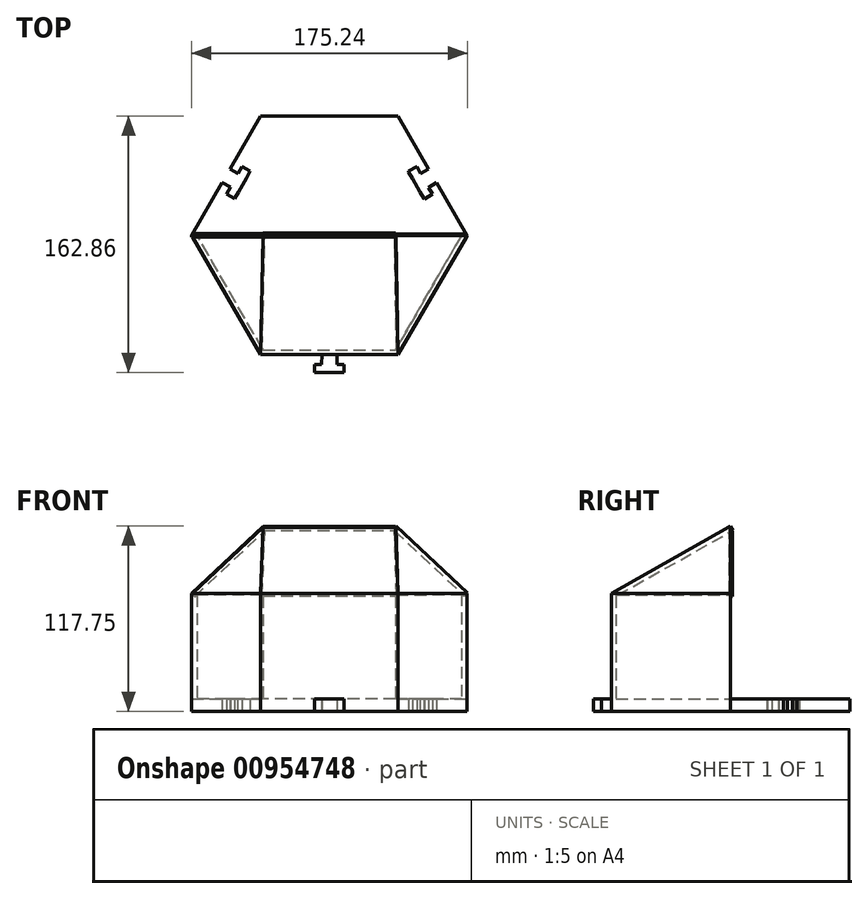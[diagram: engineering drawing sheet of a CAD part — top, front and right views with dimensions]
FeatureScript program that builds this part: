
annotation { "Feature Type Name" : "Feature", "Feature Type Description" : "" }
export const myFeature = defineFeature(function(context is Context, id is Id, definition is map)
    precondition{}
    {
        {
            var Q0;
            Q0=qCreatedBy(makeId("Top.planeOp"),FACE);
            var sketch = newSketch(context, id + "F0", { "sketchPlane" : qUnion([Q0])});
            skCircle(sketch, "E0.cCircle", {"center": v(0, 0) * mm, "radius": 75.78 * mm, "construction": true});
            skLineSegment(sketch, "E0.0", {"start": v(-43.75, 75.78) * mm, "end": v(43.75, 75.78) * mm});
            skLineSegment(sketch, "E0.1", {"start": v(43.75, 75.78) * mm, "end": v(87.5, 0) * mm});
            skLineSegment(sketch, "E0.2", {"start": v(87.5, 0) * mm, "end": v(43.75, -75.78) * mm});
            skLineSegment(sketch, "E0.3", {"start": v(43.75, -75.78) * mm, "end": v(-43.75, -75.78) * mm});
            skLineSegment(sketch, "E0.4", {"start": v(-43.75, -75.78) * mm, "end": v(-87.5, 0) * mm});
            skLineSegment(sketch, "E0.5", {"start": v(-87.5, 0) * mm, "end": v(-43.75, 75.78) * mm});
            skPoint(sketch, "E0.0.midPoint", {"position": v(0, 75.78) * mm});
            skLineSegment(sketch, "E1.0", {"start": v(-84.04, 0) * mm, "end": v(-42.02, 72.78) * mm});
            skLineSegment(sketch, "E1.1", {"start": v(42.02, 72.78) * mm, "end": v(84.04, 0) * mm});
            skLineSegment(sketch, "E1.2", {"start": v(84.04, 0) * mm, "end": v(42.02, -72.78) * mm});
            skLineSegment(sketch, "E1.3", {"start": v(-42.02, 72.78) * mm, "end": v(42.02, 72.78) * mm});
            skLineSegment(sketch, "E1.4", {"start": v(42.02, -72.78) * mm, "end": v(-42.02, -72.78) * mm});
            skLineSegment(sketch, "E1.5", {"start": v(-42.02, -72.78) * mm, "end": v(-84.04, 0) * mm});
            skLineSegment(sketch, "E2", {"start": v(-87.5, 0) * mm, "end": v(-84.04, 0) * mm});
            skLineSegment(sketch, "E3", {"start": v(84.04, 0) * mm, "end": v(87.5, 0) * mm});
            skLineSegment(sketch, "E4", {"start": v(0, 0) * mm, "end": v(0, 72.78) * mm, "construction": true});
            skLineSegment(sketch, "E5", {"start": v(0, 0) * mm, "end": v(42.02, 72.78) * mm, "construction": true});
            skLineSegment(sketch, "E6", {"start": v(0, 0) * mm, "end": v(-42.02, 72.78) * mm, "construction": true});
            skLineSegment(sketch, "E7", {"start": v(0, 36.39) * mm, "end": v(0, 72.78) * mm, "construction": true});
            skLineSegment(sketch, "E8.bottom", {"start": v(25, 48.33) * mm, "end": v(-25, 48.33) * mm});
            skLineSegment(sketch, "E8.top", {"start": v(25, 60.83) * mm, "end": v(-25, 60.83) * mm});
            skLineSegment(sketch, "E8.left", {"start": v(25, 48.33) * mm, "end": v(25, 60.83) * mm});
            skLineSegment(sketch, "E8.right", {"start": v(-25, 48.33) * mm, "end": v(-25, 60.83) * mm});
            skPoint(sketch, "E8.middle", {"position": v(0, 54.58) * mm});
            skLineSegment(sketch, "E9", {"start": v(-65.63, 37.89) * mm, "end": v(-55.16, 32) * mm, "construction": true});
            skLineSegment(sketch, "E10", {"start": v(-55.16, 32) * mm, "end": v(-52.71, 36.37) * mm, "construction": true});
            skLineSegment(sketch, "E11", {"start": v(-55.16, 32) * mm, "end": v(-57.62, 27.65) * mm, "construction": true});
            skLineSegment(sketch, "E12", {"start": v(-52.71, 36.37) * mm, "end": v(-63.12, 42.22) * mm});
            skLineSegment(sketch, "E13", {"start": v(-57.62, 27.65) * mm, "end": v(-52.71, 36.37) * mm});
            skLineSegment(sketch, "E14", {"start": v(-65.63, 37.89) * mm, "end": v(-68.13, 33.56) * mm});
            skLineSegment(sketch, "E15", {"start": v(-57.62, 27.65) * mm, "end": v(-68.13, 33.56) * mm});
            skLineSegment(sketch, "E16.MirrorCS", {"start": v(55.16, 32) * mm, "end": v(57.62, 27.65) * mm});
            skLineSegment(sketch, "E17.MirrorCS", {"start": v(55.16, 32) * mm, "end": v(52.71, 36.37) * mm});
            skLineSegment(sketch, "E18.MirrorCS", {"start": v(57.62, 27.65) * mm, "end": v(68.13, 33.56) * mm});
            skLineSegment(sketch, "E19.MirrorCS", {"start": v(87.5, 0) * mm, "end": v(43.75, 75.78) * mm});
            skLineSegment(sketch, "E20.MirrorCS", {"start": v(52.71, 36.37) * mm, "end": v(63.12, 42.22) * mm});
            skLineSegment(sketch, "E21", {"start": v(-62.87, 30.6) * mm, "end": v(-65.32, 26.25) * mm});
            skLineSegment(sketch, "E22", {"start": v(-57.62, 27.65) * mm, "end": v(-60.07, 23.3) * mm});
            skLineSegment(sketch, "E23", {"start": v(-65.32, 26.25) * mm, "end": v(-60.07, 23.3) * mm});
            skLineSegment(sketch, "E24.MirrorCS", {"start": v(-52.71, 36.37) * mm, "end": v(-50.26, 40.72) * mm});
            skLineSegment(sketch, "E25.MirrorCS", {"start": v(-57.97, 39.32) * mm, "end": v(-55.52, 43.68) * mm});
            skLineSegment(sketch, "E26.MirrorCS", {"start": v(-55.52, 43.68) * mm, "end": v(-50.26, 40.72) * mm});
            skLineSegment(sketch, "E27.MirrorCS", {"start": v(57.97, 39.32) * mm, "end": v(55.52, 43.68) * mm});
            skLineSegment(sketch, "E28.MirrorCS", {"start": v(55.52, 43.68) * mm, "end": v(50.26, 40.72) * mm});
            skLineSegment(sketch, "E29.MirrorCS", {"start": v(52.71, 36.37) * mm, "end": v(50.26, 40.72) * mm});
            skLineSegment(sketch, "E30.MirrorCS", {"start": v(57.62, 27.65) * mm, "end": v(60.07, 23.3) * mm});
            skLineSegment(sketch, "E31.MirrorCS", {"start": v(62.87, 30.6) * mm, "end": v(65.32, 26.25) * mm});
            skLineSegment(sketch, "E32.MirrorCS", {"start": v(65.32, 26.25) * mm, "end": v(60.07, 23.3) * mm});
            skLineSegment(sketch, "E33", {"start": v(-68.13, 33.56) * mm, "end": v(-65.5, 32.09) * mm});
            skLineSegment(sketch, "E34", {"start": v(68.13, 33.56) * mm, "end": v(65.5, 32.09) * mm});
            skLineSegment(sketch, "E35.1.10", {"start": v(0, 0) * mm, "end": v(-63.03, -36.39) * mm, "construction": true});
            skLineSegment(sketch, "E35.2.0", {"start": v(57.85, 27.47) * mm, "end": v(68.13, 33.56) * mm});
            skLineSegment(sketch, "E35.2.1", {"start": v(52.75, 36.07) * mm, "end": v(63.13, 42.22) * mm});
            skLineSegment(sketch, "E35.2.2", {"start": v(57.94, 39.15) * mm, "end": v(55.39, 43.45) * mm});
            skLineSegment(sketch, "E35.2.3", {"start": v(55.39, 43.45) * mm, "end": v(50.2, 40.37) * mm});
            skLineSegment(sketch, "E35.2.4", {"start": v(52.75, 36.07) * mm, "end": v(50.2, 40.37) * mm});
            skLineSegment(sketch, "E35.2.5", {"start": v(55.3, 31.77) * mm, "end": v(52.75, 36.07) * mm, "construction": true});
            skLineSegment(sketch, "E35.2.6", {"start": v(55.3, 31.77) * mm, "end": v(57.85, 27.47) * mm, "construction": true});
            skLineSegment(sketch, "E35.2.7", {"start": v(57.85, 27.47) * mm, "end": v(60.4, 23.17) * mm});
            skLineSegment(sketch, "E35.2.8", {"start": v(65.59, 26.24) * mm, "end": v(60.4, 23.17) * mm});
            skLineSegment(sketch, "E35.2.9", {"start": v(63.04, 30.54) * mm, "end": v(65.59, 26.24) * mm});
            skLineSegment(sketch, "E35.2.10", {"start": v(0, 0) * mm, "end": v(63.03, -36.39) * mm, "construction": true});
            skLineSegment(sketch, "E36.MirrorCS", {"start": v(4.88, -82.08) * mm, "end": v(9.38, -82.08) * mm});
            skLineSegment(sketch, "E37.MirrorCS", {"start": v(4.81, -87.08) * mm, "end": v(9.31, -87.08) * mm});
            skLineSegment(sketch, "E38.MirrorCS", {"start": v(0.06, -87.13) * mm, "end": v(-4.94, -87.08) * mm, "construction": true});
            skLineSegment(sketch, "E39.MirrorCS", {"start": v(-0.18, -87.02) * mm, "end": v(4.81, -87.08) * mm, "construction": true});
            skLineSegment(sketch, "E40.MirrorCS", {"start": v(9.38, -82.08) * mm, "end": v(9.31, -87.08) * mm});
            skLineSegment(sketch, "E41.MirrorCS", {"start": v(4.81, -87.08) * mm, "end": v(4.95, -75.78) * mm});
            skLineSegment(sketch, "E42.MirrorCS", {"start": v(-4.94, -87.08) * mm, "end": v(-4.8, -75.78) * mm});
            skLineSegment(sketch, "E43", {"start": v(-4.94, -87.08) * mm, "end": v(4.81, -87.08) * mm});
            skLineSegment(sketch, "E44.MirrorCS", {"start": v(-4.88, -82.08) * mm, "end": v(-9.38, -82.08) * mm});
            skLineSegment(sketch, "E45.MirrorCS", {"start": v(-4.81, -87.08) * mm, "end": v(-9.31, -87.08) * mm});
            skLineSegment(sketch, "E46.MirrorCS", {"start": v(-9.38, -82.08) * mm, "end": v(-9.31, -87.08) * mm});
            skSolve(sketch);
        }
        {
            var Q0;
            Q0=makeQuery(id+"F0.imprint","IMPRINT",FACE,{"disambiguationData":[TD([[makeQuery(id+"F0.imprint","IMPRINT",EDGE,{"derivedFrom":sQuery(id+"F0.wireOp",EDGE,"E1.0")}),-1.0]])]});
            extrude(context, id + "F1", {"entities" : qUnion([Q0]), "depth" : 8 * mm, "offsetDistance" : 25 * mm});
        }
        {
            var Q0;
            Q0=makeQuery(id+"F0.imprint","IMPRINT",FACE,{"disambiguationData":[TD([[makeQuery(id+"F0.imprint","IMPRINT",EDGE,{"derivedFrom":sQuery(id+"F0.wireOp",EDGE,"E0.2")}),-1.0]])]});
            extrude(context, id + "F2", {"entities" : qUnion([Q0]), "operationType" : NewBodyOperationType.ADD, "depth" : 75 * mm, "offsetDistance" : 25 * mm});
        }
        {
            var Q0;
            Q0=qCreatedBy(makeId("Front.planeOp"),FACE);
            var sketch = newSketch(context, id + "F3", { "sketchPlane" : qUnion([Q0])});
            skLineSegment(sketch, "E47", {"start": v(0, 0) * mm, "end": v(0, 144.27) * mm, "construction": true});
            skLineSegment(sketch, "E48", {"start": v(0, 144.27) * mm, "end": v(-94, 144.27) * mm, "construction": true});
            skLineSegment(sketch, "E49", {"start": v(0, 144.27) * mm, "end": v(81.74, 144.27) * mm});
            skLineSegment(sketch, "E50", {"start": v(0, 0) * mm, "end": v(0, 75) * mm, "construction": true});
            skLineSegment(sketch, "E51", {"start": v(0, 75) * mm, "end": v(0, 114.5) * mm, "construction": true});
            skLineSegment(sketch, "E52", {"start": v(0, 75) * mm, "end": v(-87.5, 75) * mm, "construction": true});
            skLineSegment(sketch, "E53", {"start": v(0, 114.5) * mm, "end": v(42.02, 114.5) * mm, "construction": true});
            skLineSegment(sketch, "E54", {"start": v(0, 114.5) * mm, "end": v(-42.02, 114.5) * mm});
            skLineSegment(sketch, "E55", {"start": v(0, 75) * mm, "end": v(-84.04, 75) * mm, "construction": true});
            skLineSegment(sketch, "E56", {"start": v(-42.02, 114.5) * mm, "end": v(-84.04, 75) * mm});
            skLineSegment(sketch, "E57", {"start": v(-42.02, 114.5) * mm, "end": v(-42.02, 117.5) * mm, "construction": true});
            skLineSegment(sketch, "E58", {"start": v(-42.02, 117.5) * mm, "end": v(-87.5, 75) * mm});
            skLineSegment(sketch, "E59", {"start": v(-42.02, 117.5) * mm, "end": v(0, 117.5) * mm});
            skLineSegment(sketch, "E60.MirrorCS", {"start": v(42.02, 117.5) * mm, "end": v(87.5, 75) * mm});
            skLineSegment(sketch, "E61.MirrorCS", {"start": v(42.02, 114.5) * mm, "end": v(84.04, 75) * mm});
            skLineSegment(sketch, "E62.MirrorCS", {"start": v(42.02, 117.5) * mm, "end": v(0, 117.5) * mm});
            skLineSegment(sketch, "E63.MirrorCS", {"start": v(0, 114.5) * mm, "end": v(42.02, 114.5) * mm});
            skLineSegment(sketch, "E64", {"start": v(87.5, 75) * mm, "end": v(84.04, 75) * mm});
            skLineSegment(sketch, "E65", {"start": v(-84.04, 75) * mm, "end": v(-87.5, 75) * mm});
            skSolve(sketch);
        }
        {
            var Q0;
            Q0=makeQuery(id+"F0.imprint","IMPRINT",FACE,{"disambiguationData":[TD([[makeQuery(id+"F0.imprint","IMPRINT",EDGE,{"derivedFrom":sQuery(id+"F0.wireOp",EDGE,"E0.0")}),-1.0]])]});
            extrude(context, id + "F4", {"entities" : qUnion([Q0]), "operationType" : NewBodyOperationType.ADD, "oppositeDirection" : true, "depth" : -8 * mm, "offsetDistance" : 25 * mm});
        }
        {
            var Q0;
            Q0=makeQuery(id+"F2.opExtrude","CAP_EDGE",EDGE,{"disambiguationData":[OSD([sQuery(id+"F0.wireOp",EDGE,"E0.3")])],"isStart":false});
            var Q1;
            Q1=sQuery(id+"F3.wireOp",VERTEX,"E59.end");
            cPlane(context, id + "F5", {"entities" : qUnion([Q0, Q1]), "cplaneType" : CPlaneType.LINE_ANGLE, "offset" : 25 * mm, "angle" : 0 * degree, "width" : 150 * mm, "height" : 150 * mm});
        }
        {
            var Q0;
            Q0=qCreatedBy(id+"F5.planeOp",FACE);
            var sketch = newSketch(context, id + "F6", { "sketchPlane" : qUnion([Q0])});
            skLineSegment(sketch, "E66", {"start": v(0, 29.4) * mm, "end": v(43.75, 29.4) * mm});
            skLineSegment(sketch, "E67", {"start": v(0, 29.4) * mm, "end": v(-43.75, 29.4) * mm});
            skLineSegment(sketch, "E68", {"start": v(-43.75, 29.4) * mm, "end": v(-42.02, -57.48) * mm});
            skLineSegment(sketch, "E69", {"start": v(43.75, 29.4) * mm, "end": v(42.02, -57.48) * mm});
            skLineSegment(sketch, "E70", {"start": v(-42.02, -57.48) * mm, "end": v(42.02, -57.48) * mm});
            skSolve(sketch);
        }
        {
            var Q0;
            Q0=makeQuery(id+"F6.imprint","IMPRINT",FACE,{"disambiguationData":[TD([[makeQuery(id+"F6.imprint","IMPRINT",EDGE,{"derivedFrom":sQuery(id+"F6.wireOp",EDGE,"E66")}),-1.0]])]});
            extrude(context, id + "F7", {"entities" : qUnion([Q0]), "operationType" : NewBodyOperationType.ADD, "depth" : 3 * mm, "offsetDistance" : 25 * mm});
        }
        {
            var Q0;
            Q0=makeQuery(id+"F3.imprint","IMPRINT",FACE,{"disambiguationData":[TD([[makeQuery(id+"F3.imprint","IMPRINT",EDGE,{"derivedFrom":sQuery(id+"F3.wireOp",EDGE,"E54")}),-1.0]])]});
            extrude(context, id + "F8", {"entities" : qUnion([Q0]), "operationType" : NewBodyOperationType.ADD, "depth" : 1 * mm, "offsetDistance" : 25 * mm});
        }
        {
            var Q0;
            Q0=makeQuery(id+"F8.opExtrude","CAP_EDGE",EDGE,{"disambiguationData":[OSD([sQuery(id+"F3.wireOp",EDGE,"E58")])],"isStart":true});
            var Q1;
            Q1=makeQuery(id+"F7.boolean.opBoolean","MERGE",VERTEX,{"derivedFrom":[makeQuery(id+"F2.opExtrude","CAP_VERTEX",VERTEX,{"disambiguationData":[OSD([sQuery(id+"F0.wireOp",EDGE,"E0.3"),sQuery(id+"F0.wireOp",EDGE,"E0.4")])],"isStart":false}),makeQuery(id+"F7.opExtrude","CAP_VERTEX",VERTEX,{"disambiguationData":[OSD([sQuery(id+"F6.wireOp",EDGE,"E67"),sQuery(id+"F6.wireOp",EDGE,"E68")])],"isStart":true})]});
            cPlane(context, id + "F9", {"entities" : qUnion([Q0, Q1]), "cplaneType" : CPlaneType.LINE_ANGLE, "offset" : 25 * mm, "angle" : 0 * degree, "width" : 150 * mm, "height" : 150 * mm});
        }
        {
            var Q0;
            Q0=qCreatedBy(id+"F9.planeOp",FACE);
            var sketch = newSketch(context, id + "F10", { "sketchPlane" : qUnion([Q0])});
            skLineSegment(sketch, "E71", {"start": v(-25.66, 35.61) * mm, "end": v(30.99, -31.08) * mm});
            skLineSegment(sketch, "E72", {"start": v(-25.66, 35.61) * mm, "end": v(33.23, 55.79) * mm});
            skLineSegment(sketch, "E73", {"start": v(33.23, 55.79) * mm, "end": v(30.99, -31.08) * mm});
            skSolve(sketch);
        }
        {
            var Q0;
            Q0=qSketchRegion(id+"F10",true);
            extrude(context, id + "F11", {"entities" : qUnion([Q0]), "operationType" : NewBodyOperationType.ADD, "depth" : -3 * mm, "offsetDistance" : 25 * mm});
        }
        {
            var Q0;
            Q0=makeQuery(id+"F8.opExtrude","CAP_EDGE",EDGE,{"disambiguationData":[OSD([sQuery(id+"F3.wireOp",EDGE,"E60.MirrorCS")])],"isStart":false});
            var Q1;
            Q1=makeQuery(id+"F7.boolean.opBoolean","MERGE",VERTEX,{"derivedFrom":[makeQuery(id+"F2.opExtrude","CAP_VERTEX",VERTEX,{"disambiguationData":[OSD([sQuery(id+"F0.wireOp",EDGE,"E0.2"),sQuery(id+"F0.wireOp",EDGE,"E0.3")])],"isStart":false}),makeQuery(id+"F7.opExtrude","CAP_VERTEX",VERTEX,{"disambiguationData":[OSD([sQuery(id+"F6.wireOp",EDGE,"E66"),sQuery(id+"F6.wireOp",EDGE,"E69")])],"isStart":true})]});
            cPlane(context, id + "F12", {"entities" : qUnion([Q0, Q1]), "cplaneType" : CPlaneType.LINE_ANGLE, "offset" : 25 * mm, "angle" : 0 * degree, "width" : 150 * mm, "height" : 150 * mm});
        }
        {
            var Q0;
            Q0=qCreatedBy(id+"F12.planeOp",FACE);
            var sketch = newSketch(context, id + "F13", { "sketchPlane" : qUnion([Q0])});
            skLineSegment(sketch, "E74", {"start": v(-32.88, -56.36) * mm, "end": v(25.94, -35.98) * mm});
            skLineSegment(sketch, "E75", {"start": v(25.94, -35.98) * mm, "end": v(-30.94, 30.51) * mm});
            skLineSegment(sketch, "E76", {"start": v(-30.94, 30.51) * mm, "end": v(-32.88, -56.36) * mm});
            skSolve(sketch);
        }
        {
            var Q0;
            Q0=qSketchRegion(id+"F13",true);
            extrude(context, id + "F14", {"entities" : qUnion([Q0]), "operationType" : NewBodyOperationType.ADD, "depth" : 3 * mm, "offsetDistance" : 25 * mm});
        }
        {
            var Q0;
            Q0=makeQuery(id+"F0.imprint","IMPRINT",FACE,{"disambiguationData":[TD([[makeQuery(id+"F0.imprint","IMPRINT",EDGE,{"derivedFrom":sQuery(id+"F0.wireOp",EDGE,"E8.bottom")}),-1.0]])]});
            extrude(context, id + "F15", {"entities" : qUnion([Q0]), "operationType" : NewBodyOperationType.ADD, "depth" : 8 * mm, "offsetDistance" : 25 * mm});
        }
        {
            var Q0;
            {var subQ5=sQuery(id+"F0.wireOp",EDGE,"E13");Q0=makeQuery(id+"F0.imprint","IMPRINT",FACE,{"disambiguationData":[TD([[makeQuery(id+"F0.imprint","IMPRINT",EDGE,{"derivedFrom":subQ5}),1.0]])]});}
            var Q1;
            {var subQ5=sQuery(id+"F0.wireOp",EDGE,"ALQEQqr1-oKlR-f4O9-fg5D-6GHPOLekQC52");Q1=makeQuery(id+"F0.imprint","IMPRINT",FACE,{"disambiguationData":[TD([[makeQuery(id+"F0.imprint","IMPRINT",EDGE,{"derivedFrom":subQ5}),-1.0]])]});}
            extrude(context, id + "F16", {"entities" : qUnion([Q0, Q1]), "operationType" : NewBodyOperationType.REMOVE, "oppositeDirection" : true, "depth" : 25 * mm, "offsetDistance" : 25 * mm});
        }
        {
            var Q0;
            {var subQ0=sQuery(id+"F0.wireOp",EDGE,"E2");Q0=makeQuery(id+"F0.imprint","IMPRINT",FACE,{"disambiguationData":[TD([[makeQuery(id+"F0.imprint","IMPRINT",EDGE,{"derivedFrom":subQ0}),1.0]])]});}
            var Q1;
            {var subQ0=sQuery(id+"F0.wireOp",EDGE,"E3");Q1=makeQuery(id+"F0.imprint","IMPRINT",FACE,{"disambiguationData":[TD([[makeQuery(id+"F0.imprint","IMPRINT",EDGE,{"derivedFrom":subQ0}),1.0]])]});}
            extrude(context, id + "F17", {"entities" : qUnion([Q0, Q1]), "operationType" : NewBodyOperationType.ADD, "depth" : 8 * mm, "offsetDistance" : 25 * mm});
        }
        {
            var Q0;
            Q0=makeQuery(id+"F0.imprint","IMPRINT",FACE,{"disambiguationData":[TD([[makeQuery(id+"F0.imprint","IMPRINT",EDGE,{"derivedFrom":sQuery(id+"F0.wireOp",EDGE,"e714e7f0-6398-41e4-850b-a99ada1e58f06.MirrorCS")}),1.0]])]});
            var Q1;
            {var subQ4=sQuery(id+"F0.wireOp",EDGE,"E43");Q1=makeQuery(id+"F0.imprint","IMPRINT",FACE,{"disambiguationData":[TD([[makeQuery(id+"F0.imprint","IMPRINT",EDGE,{"derivedFrom":subQ4}),1.0]])]});}
            var Q2;
            {var subQ0=sQuery(id+"F0.wireOp",EDGE,"E36.MirrorCS");Q2=makeQuery(id+"F0.imprint","IMPRINT",FACE,{"disambiguationData":[TD([[makeQuery(id+"F0.imprint","IMPRINT",EDGE,{"derivedFrom":subQ0}),-1.0]])]});}
            extrude(context, id + "F18", {"entities" : qUnion([Q0, Q1, Q2]), "operationType" : NewBodyOperationType.ADD, "depth" : 8 * mm, "offsetDistance" : 25 * mm});
        }
        {
            var Q0;
            {var subQ3=sQuery(id+"F0.wireOp",EDGE,"E44.MirrorCS");Q0=makeQuery(id+"F0.imprint","IMPRINT",FACE,{"disambiguationData":[TD([[makeQuery(id+"F0.imprint","IMPRINT",EDGE,{"derivedFrom":subQ3}),1.0]])]});}
            extrude(context, id + "F19", {"entities" : qUnion([Q0]), "operationType" : NewBodyOperationType.ADD, "depth" : 8 * mm, "offsetDistance" : 25 * mm});
        }
    });
